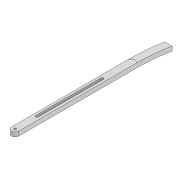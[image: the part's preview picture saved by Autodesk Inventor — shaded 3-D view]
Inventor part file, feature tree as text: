
AUTODESK INVENTOR PART (.ipt)
format: ipt  version: 2022 (Build 260153000, 153)  size: 125,952 bytes
history: native  units: mm
features: extrude x3, sketch x3, projected_geometry x2, fillet x1
ambient origin geometry x8: Origin, YZ Plane, XZ Plane, XY Plane, X Axis, Y Axis, Z Axis, Center Point
bodies: Solid1 (feature_tree)
feature tree (9):
  extrude  "Extrusion1"  Depth=10.0mm
  extrude  "Extrusion2"  Depth=120.0mm
  fillet  "Fillet1"  Radius=120.0mm
  extrude  "Extrusion3"  Depth=10.0mm TaperAngle=0.0deg
  sketch  "Sketch1"  dims[d0=160.0mm d1=10.0mm]
  sketch  "Sketch2"  dims[d2=3.3mm d3=30.0mm d5=120.0mm]
  projected_geometry  "Projected Loop1"
  projected_geometry  "Projected Loop2"
  sketch  "Sketch3"  dims[d6=3.3mm d7=6.0mm d8=0.0mm d9=6.0mm d10=373.775mm d11=90.0mm d12=10.0mm d13=0.0mm d14=2.0mm d15=100.0mm d16=0.0mm]
